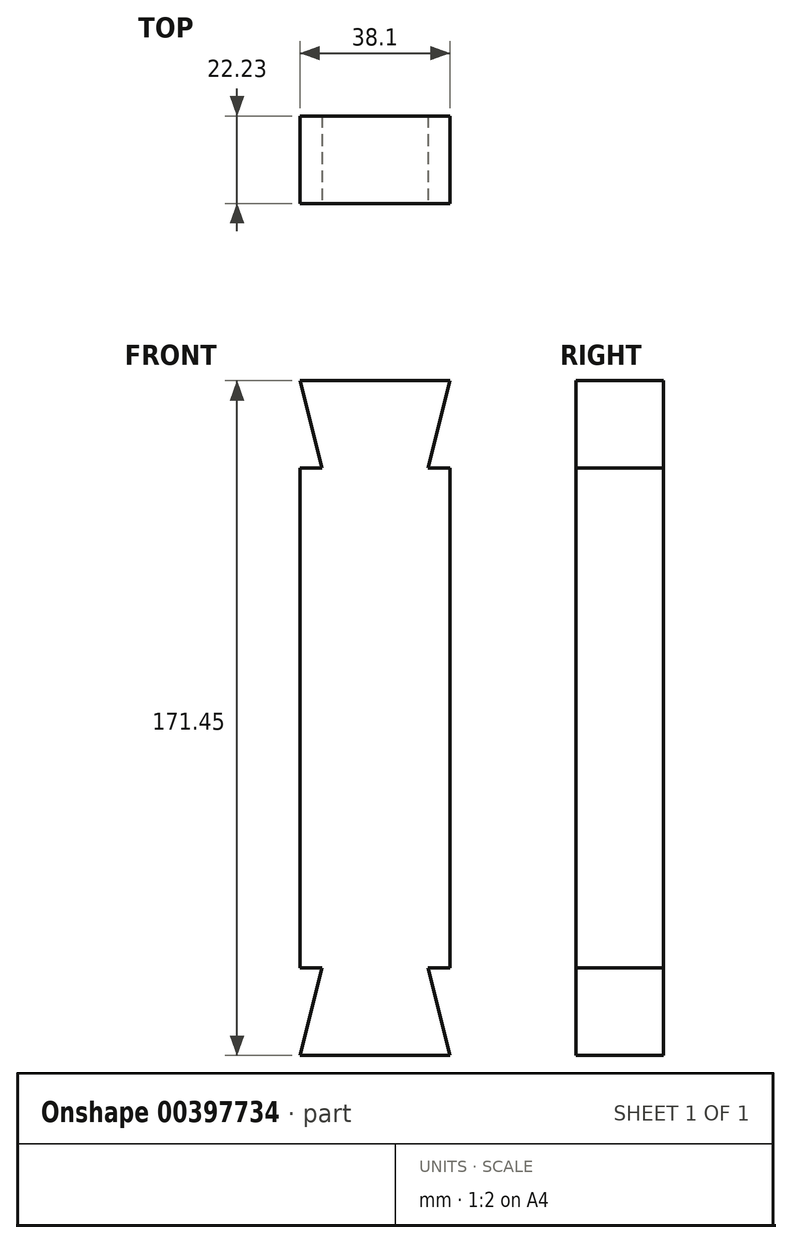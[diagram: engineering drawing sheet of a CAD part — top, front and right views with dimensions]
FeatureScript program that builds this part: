
annotation { "Feature Type Name" : "Feature", "Feature Type Description" : "" }
export const myFeature = defineFeature(function(context is Context, id is Id, definition is map)
    precondition{}
    {
        {
            var Q0;
            Q0=qCreatedBy(makeId("Front.planeOp"),FACE);
            var sketch = newSketch(context, id + "F0", { "sketchPlane" : qUnion([Q0])});
            skLineSegment(sketch, "E0.left", {"start": v(0, 0) * mm, "end": v(0, 174.63) * mm});
            skLineSegment(sketch, "E0.right", {"start": v(38.1, 0) * mm, "end": v(38.1, 174.63) * mm});
            skLineSegment(sketch, "E1.top", {"start": v(0, 174.63) * mm, "end": v(38.1, 174.63) * mm});
            skLineSegment(sketch, "E2.bottom", {"start": v(0, 0) * mm, "end": v(38.1, 0) * mm});
            skPoint(sketch, "E3.orphan", {"position": v(0, 0) * mm});
            skSolve(sketch);
        }
        {
            var Q0;
            Q0=makeQuery(id+"F0.imprint","IMPRINT",FACE,{"disambiguationData":[TD([[makeQuery(id+"F0.imprint","IMPRINT",EDGE,{"derivedFrom":sQuery(id+"F0.wireOp",EDGE,"E0.left")}),-1.0]])]});
            extrude(context, id + "F1", {"entities" : qUnion([Q0]), "depth" : 22.22 * mm});
        }
        {
            var Q0;
            Q0=makeQuery(id+"F1.opExtrude","CAP_FACE",FACE,{"disambiguationData":[OSD([sQuery(id+"F0.wireOp",EDGE,"E0.left"),sQuery(id+"F0.wireOp",EDGE,"E0.right"),sQuery(id+"F0.wireOp",EDGE,"E1.top"),sQuery(id+"F0.wireOp",EDGE,"E2.bottom")])],"isStart":false});
            var sketch = newSketch(context, id + "F2", { "sketchPlane" : qUnion([Q0])});
            skLineSegment(sketch, "E4", {"start": v(0, 173.04) * mm, "end": v(38.1, 173.04) * mm, "construction": true});
            skLineSegment(sketch, "E5", {"start": v(0, 173.04) * mm, "end": v(5.54, 150.81) * mm});
            skLineSegment(sketch, "E6", {"start": v(5.54, 150.81) * mm, "end": v(0, 150.81) * mm});
            skLineSegment(sketch, "E7", {"start": v(0, 150.81) * mm, "end": v(0, 173.04) * mm});
            skLineSegment(sketch, "E8", {"start": v(32.56, 150.81) * mm, "end": v(38.1, 173.04) * mm});
            skLineSegment(sketch, "E9", {"start": v(38.1, 150.81) * mm, "end": v(32.56, 150.81) * mm});
            skLineSegment(sketch, "E10", {"start": v(5.54, 150.81) * mm, "end": v(32.56, 150.81) * mm, "construction": true});
            skLineSegment(sketch, "E11", {"start": v(5.54, 23.81) * mm, "end": v(32.56, 23.81) * mm, "construction": true});
            skLineSegment(sketch, "E12", {"start": v(0, 1.59) * mm, "end": v(38.1, 1.59) * mm, "construction": true});
            skLineSegment(sketch, "E13", {"start": v(38.1, 1.59) * mm, "end": v(32.56, 23.81) * mm});
            skLineSegment(sketch, "E14", {"start": v(32.56, 23.81) * mm, "end": v(38.1, 23.81) * mm});
            skLineSegment(sketch, "E15", {"start": v(0, 1.59) * mm, "end": v(5.54, 23.81) * mm});
            skLineSegment(sketch, "E16", {"start": v(5.54, 23.81) * mm, "end": v(0, 23.81) * mm});
            skLineSegment(sketch, "E17", {"start": v(0, 23.81) * mm, "end": v(0, 1.59) * mm});
            skLineSegment(sketch, "E18", {"start": v(38.1, 23.81) * mm, "end": v(38.1, 1.59) * mm});
            skSolve(sketch);
        }
        {
            var Q0;
            Q0=makeQuery(id+"F2.imprint","IMPRINT",FACE,{"disambiguationData":[TD([[makeQuery(id+"F2.imprint","IMPRINT",EDGE,{"derivedFrom":sQuery(id+"F2.wireOp",EDGE,"E5")}),-1.0]])]});
            var Q1;
            {var subQ0=sQuery(id+"F2.wireOp",EDGE,"E8");Q1=makeQuery(id+"F2.imprint","IMPRINT",FACE,{"disambiguationData":[TD([[makeQuery(id+"F2.imprint","IMPRINT",EDGE,{"derivedFrom":subQ0}),-1.0]])]});}
            var Q2;
            Q2=makeQuery(id+"F2.imprint","IMPRINT",FACE,{"disambiguationData":[TD([[makeQuery(id+"F2.imprint","IMPRINT",EDGE,{"derivedFrom":sQuery(id+"F2.wireOp",EDGE,"E15")}),1.0]])]});
            var Q3;
            Q3=makeQuery(id+"F2.imprint","IMPRINT",FACE,{"disambiguationData":[TD([[makeQuery(id+"F2.imprint","IMPRINT",EDGE,{"derivedFrom":sQuery(id+"F2.wireOp",EDGE,"E13")}),-1.0]])]});
            extrude(context, id + "F3", {"entities" : qUnion([Q0, Q1, Q2, Q3]), "operationType" : NewBodyOperationType.REMOVE, "endBound" : BoundingType.THROUGH_ALL, "oppositeDirection" : true, "depth" : 25.4 * mm});
        }
        {
            var Q0;
            Q0=makeQuery(id+"F1.opExtrude","SWEPT_FACE",FACE,{"disambiguationData":[OSD([sQuery(id+"F0.wireOp",EDGE,"E1.top")])]});
            extrude(context, id + "F4", {"entities" : qUnion([Q0]), "operationType" : NewBodyOperationType.REMOVE, "oppositeDirection" : true, "depth" : 1.59 * mm});
        }
        {
            var Q0;
            Q0=makeQuery(id+"F1.opExtrude","SWEPT_FACE",FACE,{"disambiguationData":[OSD([sQuery(id+"F0.wireOp",EDGE,"E2.bottom")])]});
            extrude(context, id + "F5", {"entities" : qUnion([Q0]), "operationType" : NewBodyOperationType.REMOVE, "oppositeDirection" : true, "depth" : 1.59 * mm});
        }
    });
